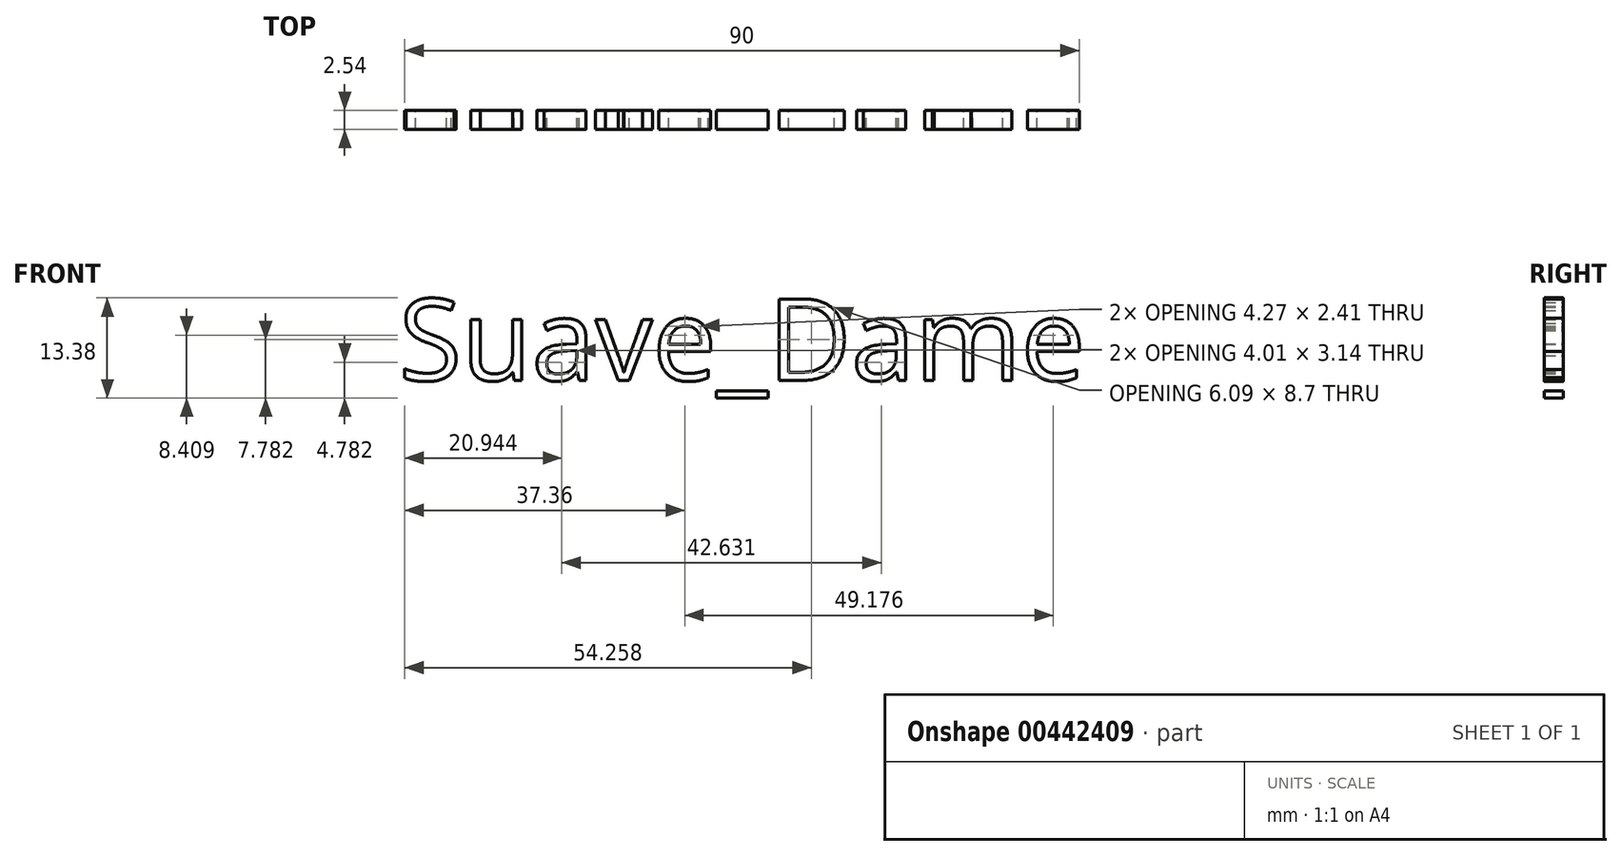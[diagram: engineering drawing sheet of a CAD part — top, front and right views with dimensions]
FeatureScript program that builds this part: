
annotation { "Feature Type Name" : "Feature", "Feature Type Description" : "" }
export const myFeature = defineFeature(function(context is Context, id is Id, definition is map)
    precondition{}
    {
        {
            var Q0;
            Q0=qCreatedBy(makeId("Front.planeOp"),FACE);
            var sketch = newSketch(context, id + "F0", { "sketchPlane" : qUnion([Q0])});
            skText(sketch, "E0", { "text": "Suave_Dame", "fontName": "OpenSans-Regular.ttf"});
            const initialGuessF0  = {"E0": [-0.0342, 0.00722, 1, 0, 0.01098]};
            skSetInitialGuess(sketch, initialGuessF0);
            skSolve(sketch);
        }
        {
            var Q0;
            Q0 = qSketchRegion(id + "F0", true);
            extrude(context, id + "F1", {"entities" : qUnion([Q0]), "depth" : 2.54 * mm});
        }
    });
